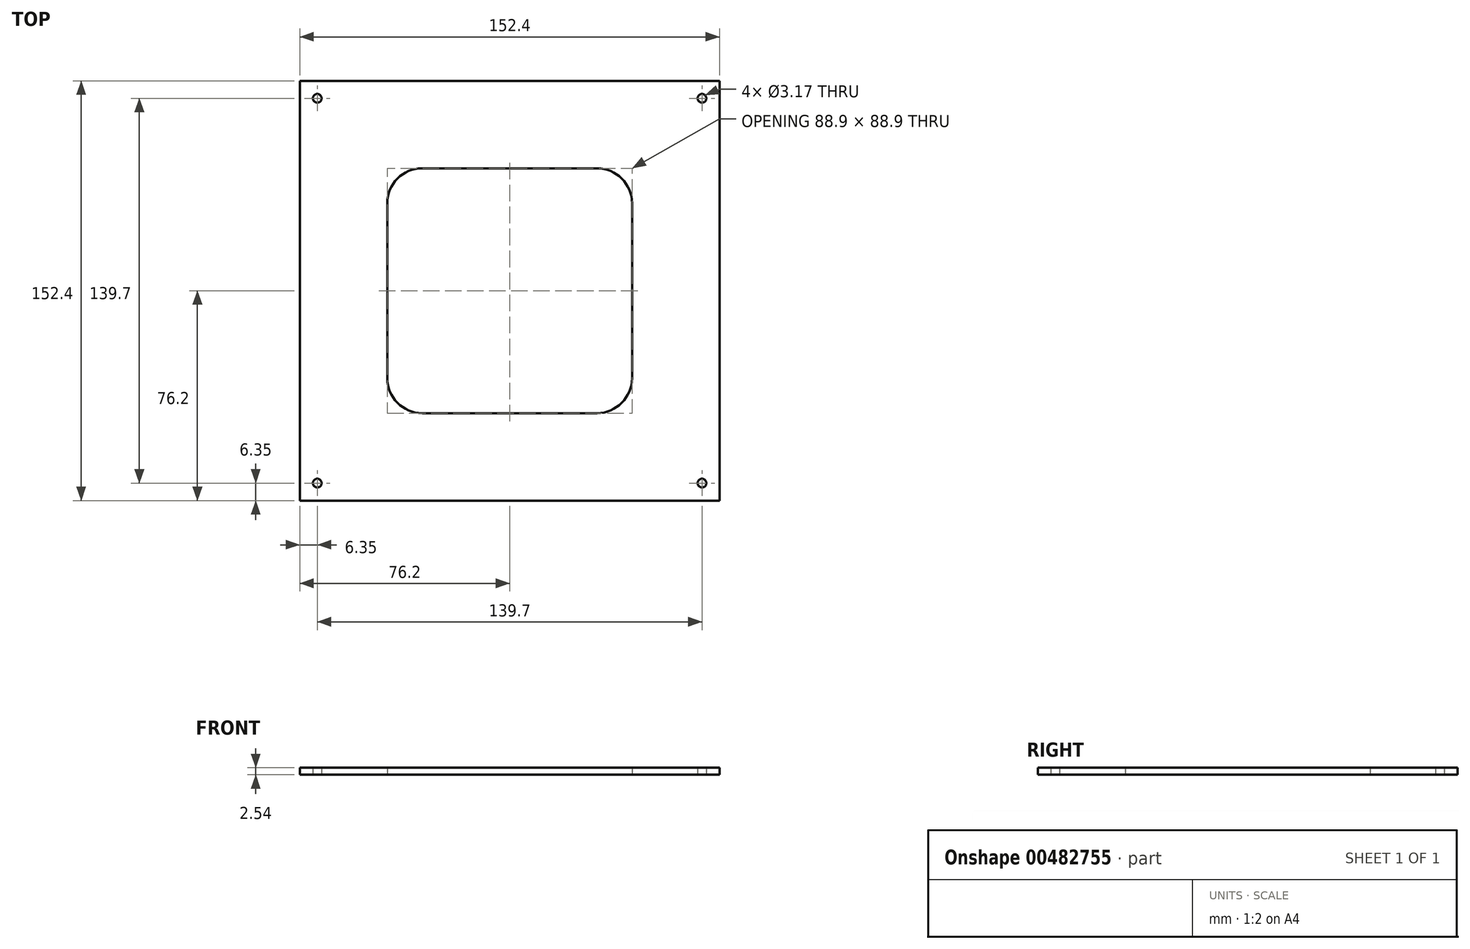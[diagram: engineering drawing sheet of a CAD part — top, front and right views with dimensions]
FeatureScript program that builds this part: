
annotation { "Feature Type Name" : "Feature", "Feature Type Description" : "" }
export const myFeature = defineFeature(function(context is Context, id is Id, definition is map)
    precondition{}
    {
        {
            var Q0;
            Q0=qCreatedBy(makeId("Top.planeOp"),FACE);
            var sketch = newSketch(context, id + "F0", { "sketchPlane" : qUnion([Q0])});
            skLineSegment(sketch, "E0.bottom", {"start": v(76.2, 76.2) * mm, "end": v(-76.2, 76.2) * mm});
            skLineSegment(sketch, "E0.top", {"start": v(76.2, -76.2) * mm, "end": v(-76.2, -76.2) * mm});
            skLineSegment(sketch, "E0.left", {"start": v(76.2, 76.2) * mm, "end": v(76.2, -76.2) * mm});
            skLineSegment(sketch, "E0.right", {"start": v(-76.2, 76.2) * mm, "end": v(-76.2, -76.2) * mm});
            skPoint(sketch, "E0.middle", {"position": v(0, 0) * mm});
            skLineSegment(sketch, "E1.bottom", {"start": v(-31.75, 44.45) * mm, "end": v(31.75, 44.45) * mm});
            skLineSegment(sketch, "E1.top", {"start": v(-31.75, -44.45) * mm, "end": v(31.75, -44.45) * mm});
            skLineSegment(sketch, "E1.left", {"start": v(-44.45, 31.75) * mm, "end": v(-44.45, -31.75) * mm});
            skLineSegment(sketch, "E1.right", {"start": v(44.45, 31.75) * mm, "end": v(44.45, -31.75) * mm});
            skPoint(sketch, "E2.visualSharp", {"position": v(-44.45, 44.45) * mm});
            skArc(sketch, "E2.filletArc", {"start": v(-31.75, 44.45) * mm, "mid": v(-40.73, 40.73) * mm, "end": v(-44.45, 31.75) * mm});
            skPoint(sketch, "E3.visualSharp", {"position": v(44.45, 44.45) * mm});
            skArc(sketch, "E3.filletArc", {"start": v(44.45, 31.75) * mm, "mid": v(40.73, 40.73) * mm, "end": v(31.75, 44.45) * mm});
            skPoint(sketch, "E4.visualSharp", {"position": v(44.45, -44.45) * mm});
            skArc(sketch, "E4.filletArc", {"start": v(31.75, -44.45) * mm, "mid": v(40.73, -40.73) * mm, "end": v(44.45, -31.75) * mm});
            skPoint(sketch, "E5.visualSharp", {"position": v(-44.45, -44.45) * mm});
            skArc(sketch, "E5.filletArc", {"start": v(-44.45, -31.75) * mm, "mid": v(-40.73, -40.73) * mm, "end": v(-31.75, -44.45) * mm});
            skCircle(sketch, "E6", {"center": v(-69.85, 69.85) * mm, "radius": 1.59 * mm});
            skCircle(sketch, "E7", {"center": v(69.85, 69.85) * mm, "radius": 1.59 * mm});
            skCircle(sketch, "E8", {"center": v(69.85, -69.85) * mm, "radius": 1.59 * mm});
            skCircle(sketch, "E9", {"center": v(-69.85, -69.85) * mm, "radius": 1.59 * mm});
            skLineSegment(sketch, "E10.bottom", {"start": v(-31.75, 57.15) * mm, "end": v(31.75, 57.15) * mm, "construction": true});
            skLineSegment(sketch, "E10.top", {"start": v(-31.75, -57.15) * mm, "end": v(31.75, -57.15) * mm, "construction": true});
            skLineSegment(sketch, "E10.left", {"start": v(-57.15, 31.75) * mm, "end": v(-57.15, -31.75) * mm, "construction": true});
            skLineSegment(sketch, "E10.right", {"start": v(57.15, 31.75) * mm, "end": v(57.15, -31.75) * mm, "construction": true});
            skArc(sketch, "E11.filletArc", {"start": v(-31.75, 57.15) * mm, "mid": v(-49.71, 49.71) * mm, "end": v(-57.15, 31.75) * mm, "construction": true});
            skArc(sketch, "E12.filletArc", {"start": v(57.15, 31.75) * mm, "mid": v(49.71, 49.71) * mm, "end": v(31.75, 57.15) * mm, "construction": true});
            skArc(sketch, "E13.filletArc", {"start": v(31.75, -57.15) * mm, "mid": v(49.71, -49.71) * mm, "end": v(57.15, -31.75) * mm, "construction": true});
            skArc(sketch, "E14.filletArc", {"start": v(-57.15, -31.75) * mm, "mid": v(-49.71, -49.71) * mm, "end": v(-31.75, -57.15) * mm, "construction": true});
            skSolve(sketch);
        }
        {
            var Q0;
            Q0 = qSketchRegion(id + "F0", true);
            extrude(context, id + "F1", {"entities" : qUnion([Q0]), "depth" : 2.54 * mm});
        }
    });
